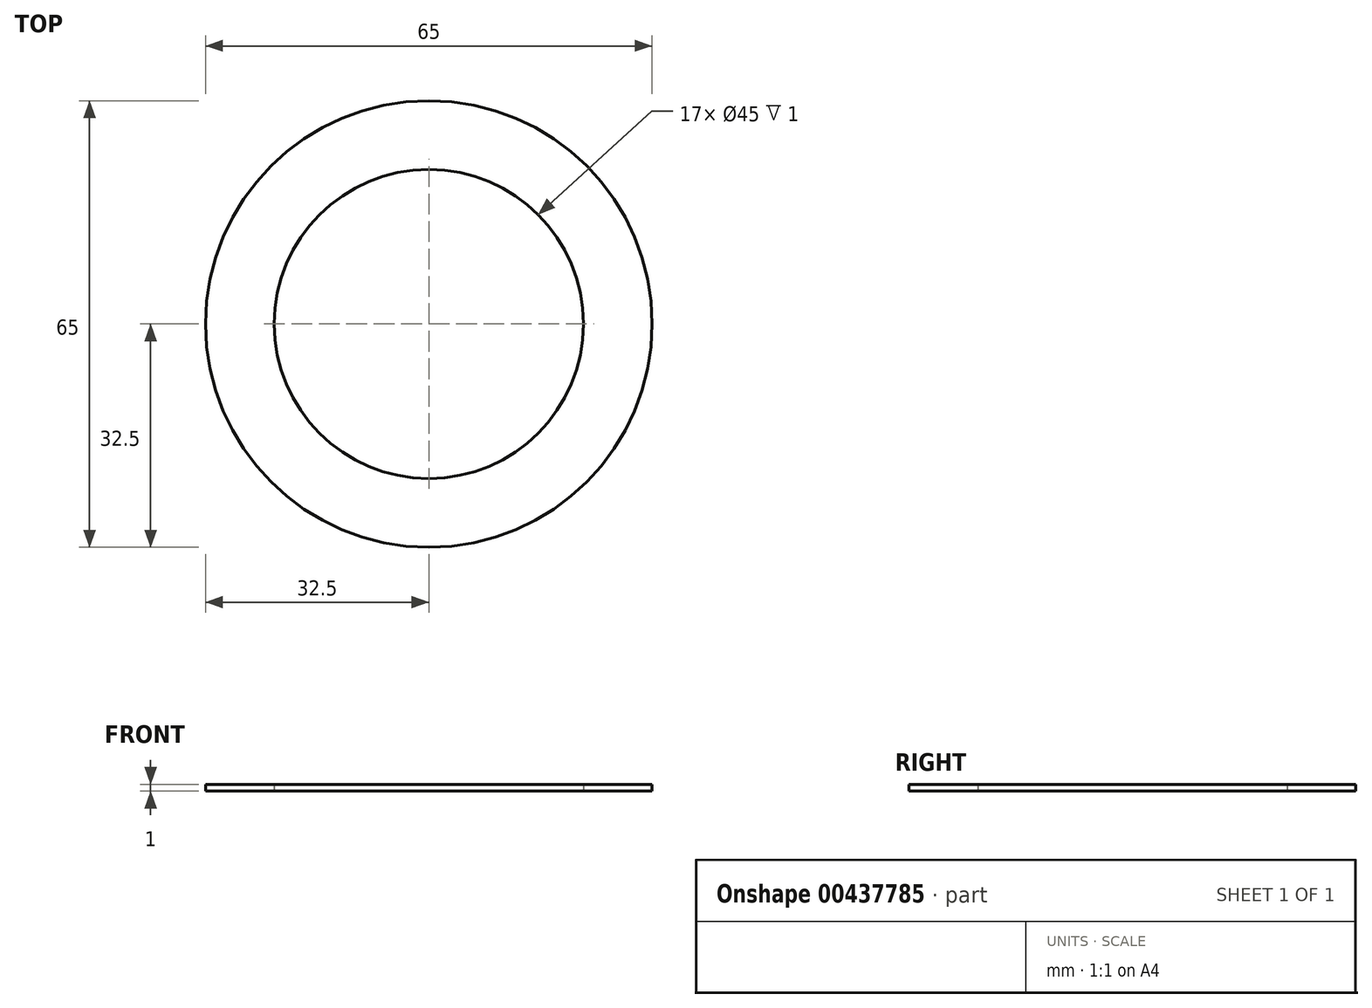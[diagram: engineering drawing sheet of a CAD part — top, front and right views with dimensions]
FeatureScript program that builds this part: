
annotation { "Feature Type Name" : "Feature", "Feature Type Description" : "" }
export const myFeature = defineFeature(function(context is Context, id is Id, definition is map)
    precondition{}
    {
        {
            var Q0;
            Q0=qCreatedBy(makeId("Top.planeOp"),FACE);
            var sketch = newSketch(context, id + "F0", { "sketchPlane" : qUnion([Q0])});
            skCircle(sketch, "E0", {"center": v(0, 0) * mm, "radius": 22.5 * mm});
            skCircle(sketch, "E1", {"center": v(0, 0) * mm, "radius": 32.5 * mm});
            skSolve(sketch);
        }
        {
            var Q0;
            Q0 = qSketchRegion(id + "F0", true);
            extrude(context, id + "F1", {"entities" : qUnion([Q0]), "depth" : 1 * mm});
        }
    });
